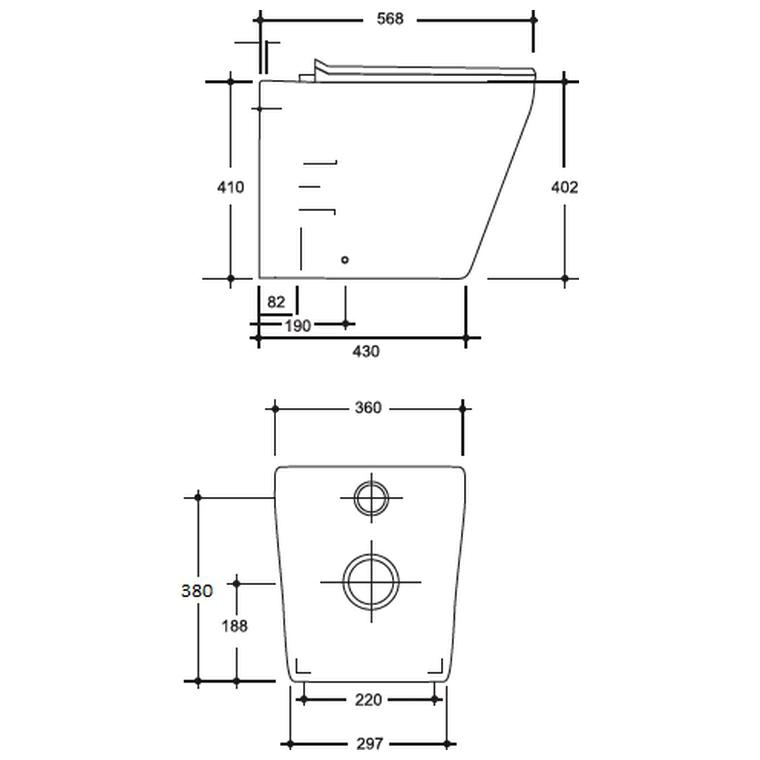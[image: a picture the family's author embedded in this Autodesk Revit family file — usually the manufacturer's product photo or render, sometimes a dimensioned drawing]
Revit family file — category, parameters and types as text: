
# Revit family: LIXIL - 772664WH - COBRA WELCOME TOILET CLOSE COUPLE SUITE
name_source: partatom
category: Plumbing Fixtures
units: mm (PartAtom-declared; Revit-internal decimal feet)

## family parameters
Always vertical = Yes
Cut with Voids When Loaded = No
Enable Cutting in Views = No
Maintain Annotation Orientation = No
OmniClass Number = 23.45.00.00
OmniClass Title = Sanitary, Laundry, and Cleaning Equipment
Part Type = Normal
Room Calculation Point = No
Round Connector Dimension = Use Diameter
Shared = Yes
Work Plane-Based = No

## types (1)
- 772664WH
    Default Elevation = 0 mm  [stored 0 ft]
    Description = Cobra Welcome wc to detail and spec. See sanware schedule. Available from Lixil.
    Hosted on lixil.co.za = https://www.lixil.co.za
    M _ CISTERN = M _ LIXIL - VAAL - PORCELAIN - WHITE 01
    M _ WC = M _ LIXIL - VAAL - PORCELAIN - WHITE 01
    M _ WC LID AND SEAT = M _ LIXIL - VAAL - PLASTIC - WHITE 01
    M _ WC SEAT SS FITTINGS = M _ LIXIL - STAINLESS STEEL 01
    M _ WC SEAT SUPPORT = M _ LIXIL - VAAL - PLASTIC - WHITE 01
    Product Specification = Supplier: Lixil.
Product description: Cobra Welcome Close coupled toilet suite. Top, dual flush capability with 3L and 6L flush available. Box rim. Package includes cistern and cistern fittings, pan, seat and cover, connector and installation manual. Cistern manufactured with left hand side inlet hole only as per European standard.
10 Year Warranty Cobra Genuine Cobra TeamAssist.
Product Code: CWLCCST1-6DT01.
SKU Code	: 772664WH.
Barcode: 6002194040477. 
Brand: Cobra.
Range: Welcome.
Category: Toilets.
Sub-Category: Close-Coupled Suites.
Material: Ceramic.
Colour: White.
Package Height: 510 mm
Package Width: 460 mm
Package Length: 950 mm
Product Height: 790 mm
Product Width: 430 mm
Product Length: 660 mm
Package Volume: 222870000 mm³
Package Weight: 43.05 kg

Notes:
- Refer to manufacturer's and supplier's installation, maintenance and cleaning manual.
- Refer to manufacturer's and supplier's guarantees and warrantees document.

note: [stored X ft] marks values corroborated as IEEE doubles in the binary element streams (Revit-internal decimal feet)

## geometry (parser evidence)
native form markers: Sweep x26
no freeform markers — native parametric forms only
